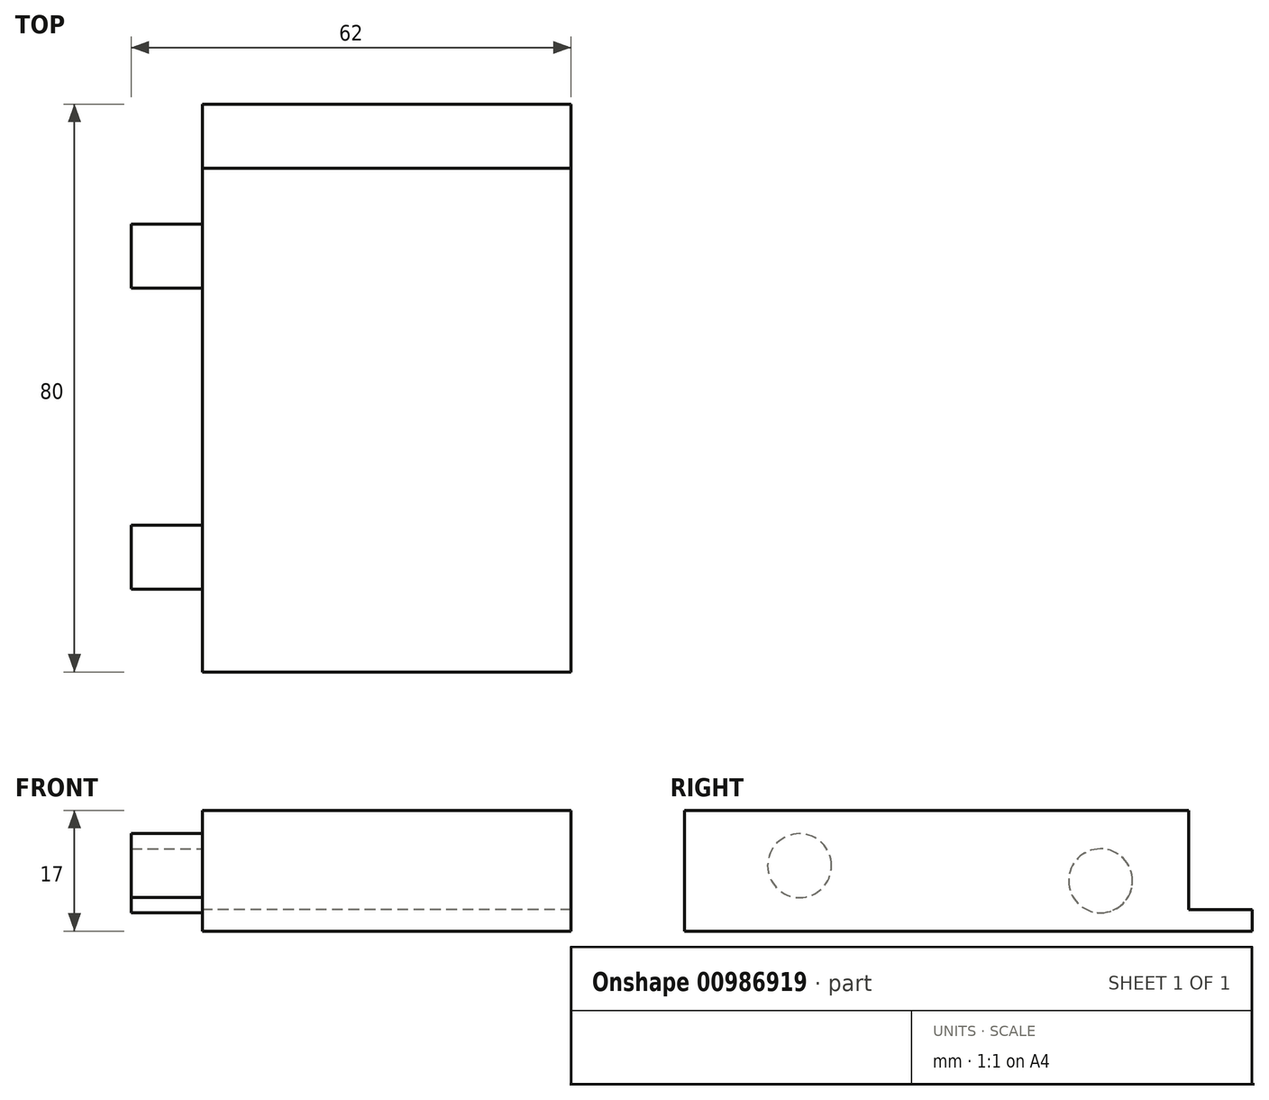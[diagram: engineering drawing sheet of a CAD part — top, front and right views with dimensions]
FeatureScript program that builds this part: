
annotation { "Feature Type Name" : "Feature", "Feature Type Description" : "" }
export const myFeature = defineFeature(function(context is Context, id is Id, definition is map)
    precondition{}
    {
        {
            var Q0;
            Q0=qCreatedBy(makeId("Top.planeOp"),FACE);
            var sketch = newSketch(context, id + "F0", { "sketchPlane" : qUnion([Q0])});
            skLineSegment(sketch, "E0.bottom", {"start": v(26, 40) * mm, "end": v(-26, 40) * mm});
            skLineSegment(sketch, "E0.top", {"start": v(26, -40) * mm, "end": v(-26, -40) * mm});
            skLineSegment(sketch, "E0.left", {"start": v(26, 40) * mm, "end": v(26, -40) * mm});
            skLineSegment(sketch, "E0.right", {"start": v(-26, 40) * mm, "end": v(-26, -40) * mm});
            skPoint(sketch, "E0.middle", {"position": v(0, 0) * mm});
            skSolve(sketch);
        }
        {
            var Q0;
            Q0 = qSketchRegion(id + "F0", true);
            extrude(context, id + "F1", {"entities" : qUnion([Q0]), "depth" : 3 * mm, "offsetDistance" : 25 * mm});
        }
        {
            var Q0;
            Q0=makeQuery(id+"F1.opExtrude","CAP_FACE",FACE,{"disambiguationData":[OSD([sQuery(id+"F0.wireOp",EDGE,"E0.bottom"),sQuery(id+"F0.wireOp",EDGE,"E0.top"),sQuery(id+"F0.wireOp",EDGE,"E0.left"),sQuery(id+"F0.wireOp",EDGE,"E0.right")])],"isStart":false});
            var sketch = newSketch(context, id + "F2", { "sketchPlane" : qUnion([Q0])});
            skLineSegment(sketch, "E1.bottom", {"start": v(26, -40) * mm, "end": v(-26, -40) * mm});
            skLineSegment(sketch, "E1.top", {"start": v(26, 31) * mm, "end": v(-26, 31) * mm});
            skLineSegment(sketch, "E1.left", {"start": v(26, -40) * mm, "end": v(26, 31) * mm});
            skLineSegment(sketch, "E1.right", {"start": v(-26, -40) * mm, "end": v(-26, 31) * mm});
            skSolve(sketch);
        }
        {
            var Q0;
            Q0 = qSketchRegion(id + "F2", true);
            extrude(context, id + "F3", {"entities" : qUnion([Q0]), "operationType" : NewBodyOperationType.ADD, "depth" : 14 * mm, "offsetDistance" : 25 * mm});
        }
        {
            var Q0;
            Q0=makeQuery(id+"F3.boolean.opBoolean","MERGE",FACE,{"derivedFrom":[makeQuery(id+"F1.opExtrude","SWEPT_FACE",FACE,{"disambiguationData":[OSD([sQuery(id+"F0.wireOp",EDGE,"E0.right")])]}),makeQuery(id+"F3.opExtrude","SWEPT_FACE",FACE,{"disambiguationData":[OSD([sQuery(id+"F2.wireOp",EDGE,"E1.right")])]})]});
            var sketch = newSketch(context, id + "F4", { "sketchPlane" : qUnion([Q0])});
            skCircle(sketch, "E2", {"center": v(23.81, 9.22) * mm, "radius": 4.5 * mm});
            skCircle(sketch, "E3", {"center": v(-18.61, 7.08) * mm, "radius": 4.5 * mm});
            skSolve(sketch);
        }
        {
            var Q0;
            Q0 = qSketchRegion(id + "F4", true);
            extrude(context, id + "F5", {"entities" : qUnion([Q0]), "operationType" : NewBodyOperationType.ADD, "depth" : 10 * mm, "offsetDistance" : 25 * mm});
        }
    });
